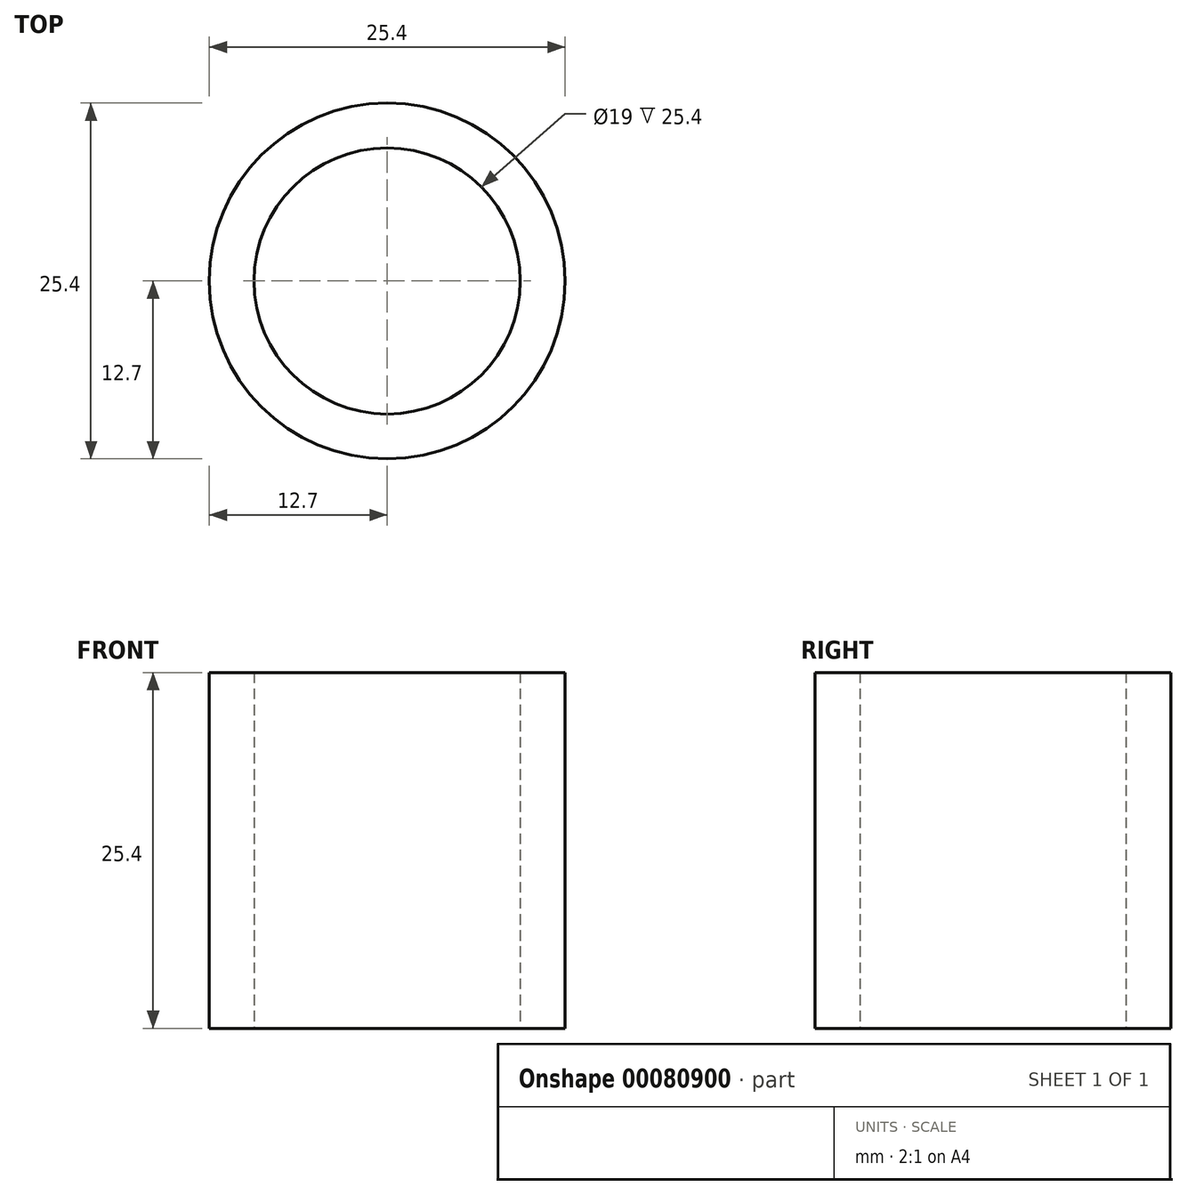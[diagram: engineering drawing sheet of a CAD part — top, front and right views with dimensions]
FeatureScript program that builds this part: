
annotation { "Feature Type Name" : "Feature", "Feature Type Description" : "" }
export const myFeature = defineFeature(function(context is Context, id is Id, definition is map)
    precondition{}
    {
        {
            var Q0;
            Q0=qCreatedBy(makeId("Top.planeOp"),FACE);
            var sketch = newSketch(context, id + "F0", { "sketchPlane" : qUnion([Q0])});
            skCircle(sketch, "E0", {"center": v(0, 0) * mm, "radius": 9.5 * mm});
            skCircle(sketch, "E1", {"center": v(0, 0) * mm, "radius": 12.7 * mm});
            skSolve(sketch);
        }
        {
            var Q0;
            Q0 = qSketchRegion(id + "F0", true);
            extrude(context, id + "F1", {"entities" : qUnion([Q0]), "depth" : 25.4 * mm});
        }
    });
